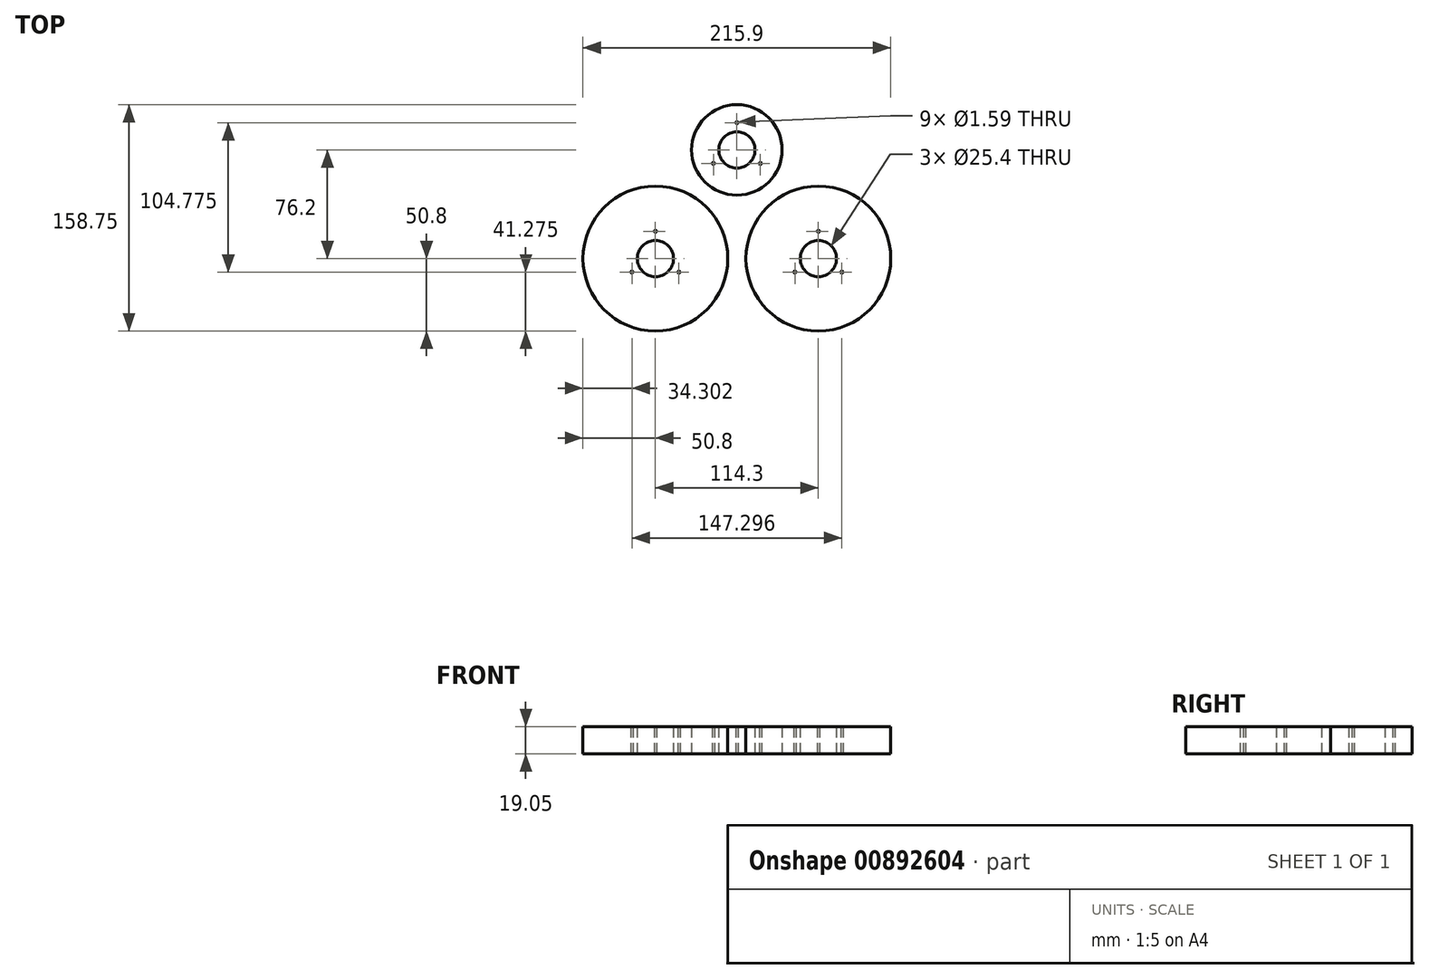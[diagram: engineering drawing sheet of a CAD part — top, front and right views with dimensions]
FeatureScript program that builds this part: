
annotation { "Feature Type Name" : "Feature", "Feature Type Description" : "" }
export const myFeature = defineFeature(function(context is Context, id is Id, definition is map)
    precondition{}
    {
        {
            var Q0;
            Q0=qCreatedBy(makeId("Top.planeOp"),FACE);
            var sketch = newSketch(context, id + "F0", { "sketchPlane" : qUnion([Q0])});
            skCircle(sketch, "E0", {"center": v(0, 0) * mm, "radius": 50.8 * mm});
            skCircle(sketch, "E1", {"center": v(57.15, 76.2) * mm, "radius": 31.75 * mm});
            skCircle(sketch, "E2", {"center": v(114.3, 0) * mm, "radius": 50.8 * mm});
            skCircle(sketch, "E3", {"center": v(0, 19.05) * mm, "radius": 0.8 * mm});
            skCircle(sketch, "E4", {"center": v(57.15, 95.25) * mm, "radius": 0.8 * mm});
            skCircle(sketch, "E5.1.0", {"center": v(40.65, 66.68) * mm, "radius": 0.8 * mm});
            skCircle(sketch, "E5.2.0", {"center": v(73.65, 66.68) * mm, "radius": 0.8 * mm});
            skCircle(sketch, "E6", {"center": v(114.3, 19.05) * mm, "radius": 0.8 * mm});
            skCircle(sketch, "E7.1.0", {"center": v(97.8, -9.52) * mm, "radius": 0.8 * mm});
            skCircle(sketch, "E7.2.0", {"center": v(130.8, -9.53) * mm, "radius": 0.8 * mm});
            skCircle(sketch, "E8.1.0", {"center": v(-16.5, -9.52) * mm, "radius": 0.8 * mm});
            skCircle(sketch, "E8.2.0", {"center": v(16.5, -9.53) * mm, "radius": 0.8 * mm});
            skCircle(sketch, "E9", {"center": v(0, 0) * mm, "radius": 12.7 * mm});
            skCircle(sketch, "E10", {"center": v(57.15, 76.2) * mm, "radius": 12.7 * mm});
            skCircle(sketch, "E11", {"center": v(114.3, 0) * mm, "radius": 12.7 * mm});
            skSolve(sketch);
        }
        {
            var Q0;
            Q0=makeQuery(id+"F0.imprint","IMPRINT",FACE,{"disambiguationData":[TD([[makeQuery(id+"F0.imprint","IMPRINT",EDGE,{"derivedFrom":sQuery(id+"F0.wireOp",EDGE,"E0")}),1.0]])]});
            var Q1;
            Q1=makeQuery(id+"F0.imprint","IMPRINT",FACE,{"disambiguationData":[TD([[makeQuery(id+"F0.imprint","IMPRINT",EDGE,{"derivedFrom":sQuery(id+"F0.wireOp",EDGE,"E2")}),1.0]])]});
            var Q2;
            Q2=makeQuery(id+"F0.imprint","IMPRINT",FACE,{"disambiguationData":[TD([[makeQuery(id+"F0.imprint","IMPRINT",EDGE,{"derivedFrom":sQuery(id+"F0.wireOp",EDGE,"E1")}),1.0]])]});
            extrude(context, id + "F1", {"entities" : qUnion([Q0, Q1, Q2]), "depth" : 19.05 * mm, "offsetDistance" : 25.4 * mm});
        }
    });
